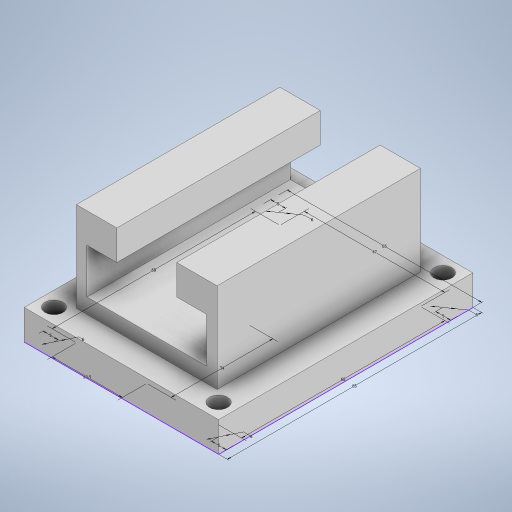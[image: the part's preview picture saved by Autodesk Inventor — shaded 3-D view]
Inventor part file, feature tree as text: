
AUTODESK INVENTOR PART (.ipt)
format: ipt  version: 2023 (Build 270158000, 158)  size: 282,112 bytes
history: native  units: mm
features: extrude x4, sketch x3
ambient origin geometry x8: Origin, YZ Plane, XZ Plane, XY Plane, X Axis, Y Axis, Z Axis, Center Point
bodies: Solid1 (feature_tree)
feature tree (7):
  sketch  "Sketch1"  dims[d0=65.0mm d1=85.0mm]
  sketch  "Sketch2"  dims[d2=34.0mm d3=23.5mm]
  extrude  "Extrusion1"  Depth=85.0mm
  extrude  "Extrusion2"  Depth=23.5mm
  extrude  "Extrusion3"  Depth=47.0mm
  extrude  "Extrusion4"  Depth=68.0mm
  sketch  "Sketch3"  dims[d4=68.0mm d5=47.0mm d6=68.0mm d8=5.0mm d9=6.0mm d11=5.0mm d12=6.0mm d14=5.0mm d15=6.0mm d17=5.0mm d18=6.0mm d19=10.0mm d20=0.0mm d21=20.0mm d22=0.0mm d23=40.0mm d24=0.0mm d25=13.5mm d26=13.5mm d27=10.0mm d28=10.0mm d29=15.0mm d30=40.0mm d31=15.0mm d32=10.0mm d33=68.0mm d34=0.0mm]
